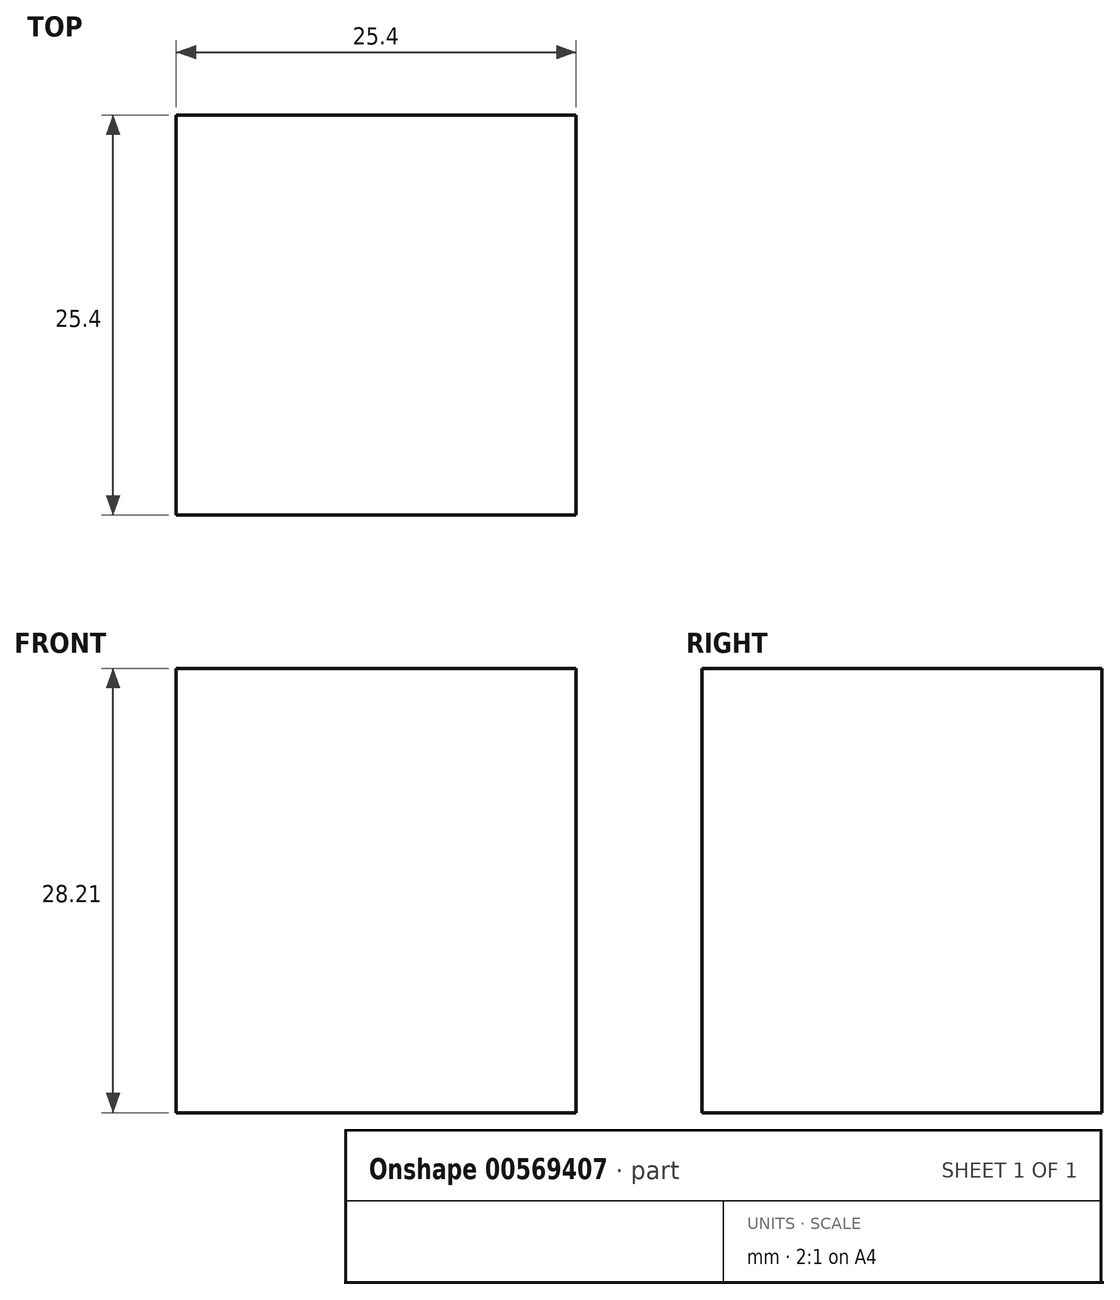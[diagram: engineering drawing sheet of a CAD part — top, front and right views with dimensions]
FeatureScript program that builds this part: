
annotation { "Feature Type Name" : "Feature", "Feature Type Description" : "" }
export const myFeature = defineFeature(function(context is Context, id is Id, definition is map)
    precondition{}
    {
        {
            var Q0;
            Q0=qCreatedBy(makeId("Front.planeOp"),FACE);
            var sketch = newSketch(context, id + "F0", { "sketchPlane" : qUnion([Q0])});
            skLineSegment(sketch, "E0.bottom", {"start": v(0, 0) * mm, "end": v(-25.4, 0) * mm});
            skLineSegment(sketch, "E0.top", {"start": v(0, 28.2) * mm, "end": v(-25.4, 28.2) * mm});
            skLineSegment(sketch, "E0.left", {"start": v(0, 0) * mm, "end": v(0, 28.2) * mm});
            skLineSegment(sketch, "E0.right", {"start": v(-25.4, 0) * mm, "end": v(-25.4, 28.2) * mm});
            skSolve(sketch);
        }
        {
            var Q0;
            Q0=makeQuery(id+"F0.imprint","IMPRINT",FACE,{"disambiguationData":[TD([[makeQuery(id+"F0.imprint","IMPRINT",EDGE,{"derivedFrom":sQuery(id+"F0.wireOp",EDGE,"E0.bottom")}),-1.0]])]});
            extrude(context, id + "F1", {"entities" : qUnion([Q0]), "depth" : 25.4 * mm, "offsetDistance" : 25.4 * mm});
        }
    });
